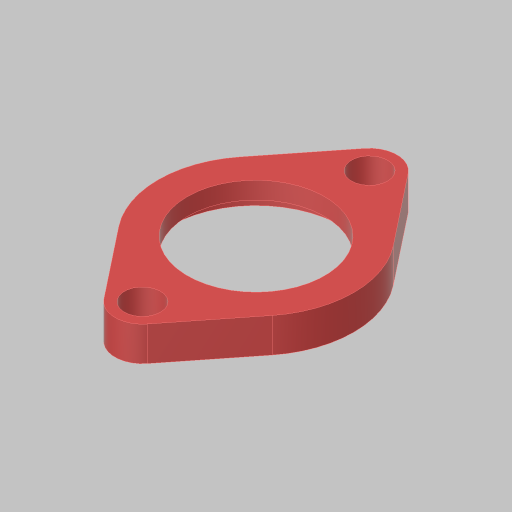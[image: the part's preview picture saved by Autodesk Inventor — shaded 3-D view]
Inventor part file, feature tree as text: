
AUTODESK INVENTOR PART (.ipt)
format: ipt  version: 2023.5 (Build 275446000, 446)  size: 124,928 bytes
history: native  units: in
note: dims shown in document units (in); Inventor stores cm internally (conversion verified against a paired STEP export)
features: extrude x2, sketch x1, hole x1
ambient origin geometry x8: Origin, YZ Plane, XZ Plane, XY Plane, X Axis, Y Axis, Z Axis, Center Point
bodies: Solid1 (feature_tree)
feature tree (4):
  sketch  "Sketch1"  dims[d0=1.0in d1=1.425in d2=0.4in d3=0.25in d4=0.0in d5=0.125in d6=0.0in d7=1.255in d8=0.2638in d9=0.38in d10=0.385in d11=0.25in d12=0.5635in d13=1.0in d14=0.8108in d15=1.655in]
  extrude  "Extrusion1"  Depth=1.425in
  extrude  "Extrusion2"  Depth=0.25in
  hole  "Hole1"  [1 undecoded]
note: 1 required parameter value undecoded (feature->parameter linkage not recoverable at this tier; creation-order binding heuristic only, values carry confidence <= 0.55)
